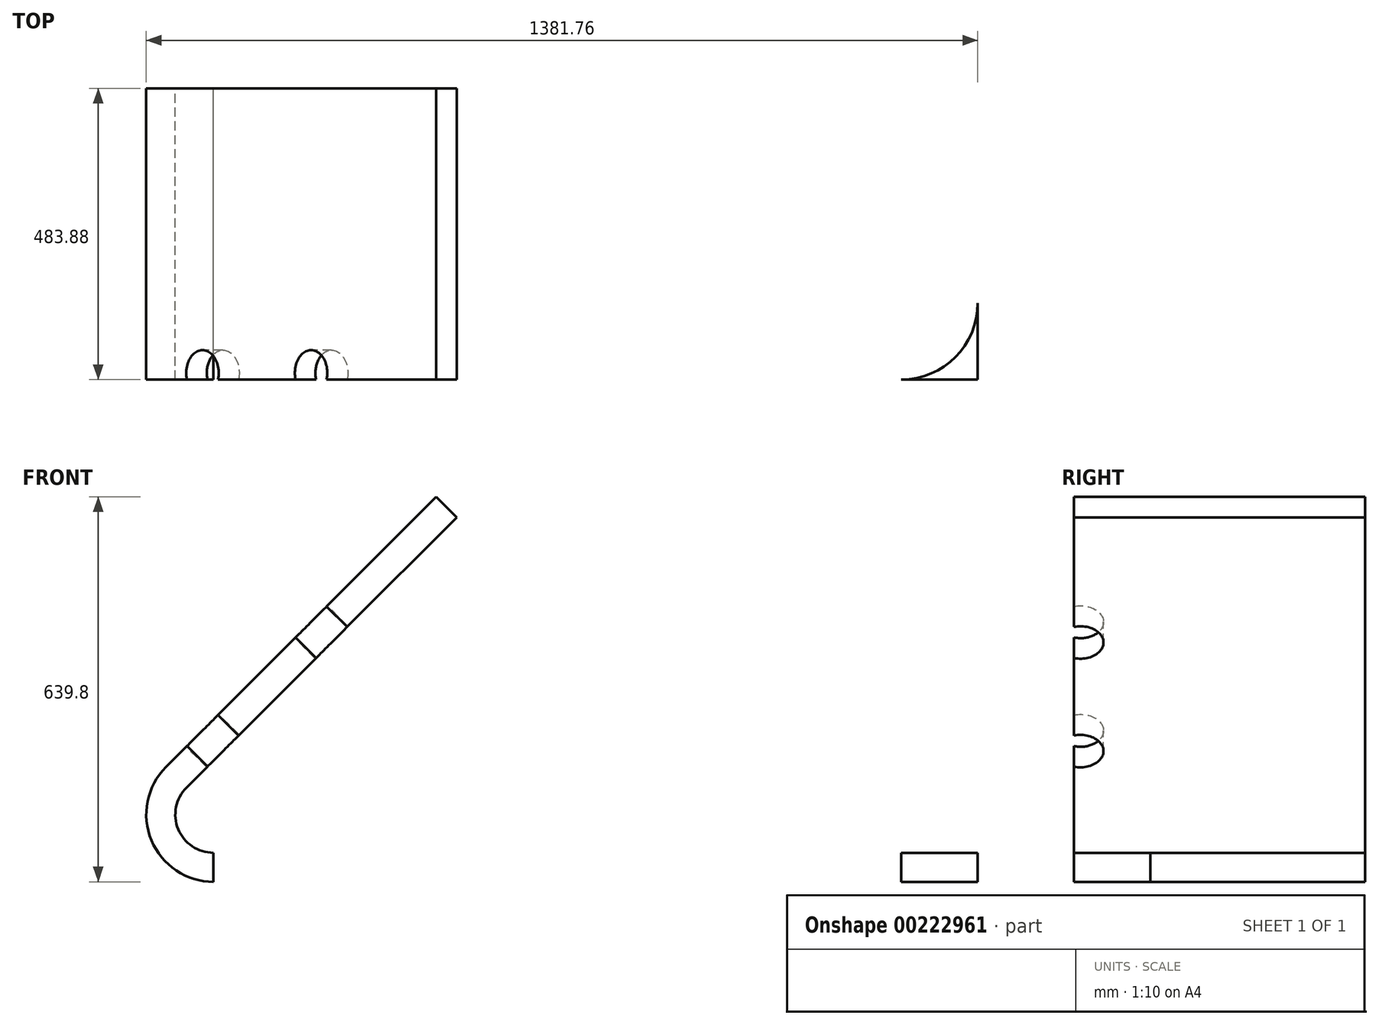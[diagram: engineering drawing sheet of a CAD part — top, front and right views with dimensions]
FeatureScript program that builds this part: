
annotation { "Feature Type Name" : "Feature", "Feature Type Description" : "" }
export const myFeature = defineFeature(function(context is Context, id is Id, definition is map)
    precondition{}
    {
        {
            var Q0;
            Q0=qCreatedBy(makeId("Front.planeOp"),FACE);
            var sketch = newSketch(context, id + "F0", { "sketchPlane" : qUnion([Q0])});
            skArc(sketch, "E0", {"start": v(-380.76, 79.03) * mm, "mid": v(-405, -42.77) * mm, "end": v(-301.74, -111.76) * mm});
            skLineSegment(sketch, "E1", {"start": v(-380.76, 79.03) * mm, "end": v(68.25, 528.04) * mm});
            skLineSegment(sketch, "E2", {"start": v(-301.74, -111.76) * mm, "end": v(968.26, -111.76) * mm});
            skLineSegment(sketch, "E3", {"start": v(968.26, -111.76) * mm, "end": v(968.26, -63.5) * mm});
            skLineSegment(sketch, "E4", {"start": v(102.37, 493.91) * mm, "end": v(68.25, 528.04) * mm});
            skLineSegment(sketch, "E5", {"start": v(968.26, -63.5) * mm, "end": v(-301.74, -63.5) * mm});
            skLineSegment(sketch, "E6", {"start": v(102.37, 493.91) * mm, "end": v(-346.64, 44.9) * mm});
            skArc(sketch, "E7", {"start": v(-346.64, 44.9) * mm, "mid": v(-360.4, -24.3) * mm, "end": v(-301.74, -63.5) * mm});
            skSolve(sketch);
        }
        {
            var Q0;
            Q0=makeQuery(id+"F0.imprint","IMPRINT",FACE,{"disambiguationData":[TD([[makeQuery(id+"F0.imprint","IMPRINT",EDGE,{"derivedFrom":sQuery(id+"F0.wireOp",EDGE,"E0")}),1.0]])]});
            extrude(context, id + "F1", {"entities" : qUnion([Q0]), "endBound" : BoundingType.SYMMETRIC, "depth" : 483.87 * mm});
        }
        {
            var Q0;
            Q0=makeQuery(id+"F1.opExtrude","SWEPT_FACE",FACE,{"disambiguationData":[OSD([sQuery(id+"F0.wireOp",EDGE,"E1")])]});
            var sketch = newSketch(context, id + "F2", { "sketchPlane" : qUnion([Q0])});
            skLineSegment(sketch, "E8", {"start": v(-325.12, -241.94) * mm, "end": v(-325.12, 241.94) * mm});
            skLineSegment(sketch, "E9", {"start": v(421.64, -241.94) * mm, "end": v(421.64, -127.64) * mm});
            skLineSegment(sketch, "E10", {"start": v(421.64, -127.64) * mm, "end": v(231.14, -127.64) * mm});
            skCircle(sketch, "E11", {"center": v(231.14, -127.64) * mm, "radius": 38.1 * mm});
            skLineSegment(sketch, "E12", {"start": v(421.64, 0) * mm, "end": v(29.41, 0) * mm});
            skCircle(sketch, "E13.MirrorC", {"center": v(231.14, 127.64) * mm, "radius": 38.1 * mm});
            skLineSegment(sketch, "E14", {"start": v(421.64, 241.94) * mm, "end": v(421.64, 114.94) * mm});
            skArc(sketch, "E15", {"start": v(421.64, 114.94) * mm, "mid": v(384.44, 204.74) * mm, "end": v(294.64, 241.94) * mm});
            skLineSegment(sketch, "E16", {"start": v(294.64, 241.94) * mm, "end": v(421.64, 241.94) * mm});
            skArc(sketch, "E17.MirrorCS", {"start": v(421.64, -114.94) * mm, "mid": v(384.44, -204.74) * mm, "end": v(294.64, -241.94) * mm});
            skLineSegment(sketch, "E18.MirrorCS", {"start": v(421.64, -241.94) * mm, "end": v(421.64, -114.94) * mm});
            skLineSegment(sketch, "E19.MirrorCS", {"start": v(294.64, -241.94) * mm, "end": v(421.64, -241.94) * mm});
            skSolve(sketch);
        }
        {
            var Q0;
            Q0 = qSketchRegion(id + "F2", true);
            extrude(context, id + "F3", {"entities" : qUnion([Q0]), "operationType" : NewBodyOperationType.REMOVE, "oppositeDirection" : true, "depth" : 63.5 * mm});
        }
        {
            var Q0;
            Q0=makeQuery(id+"F1.opExtrude","SWEPT_FACE",FACE,{"disambiguationData":[OSD([sQuery(id+"F0.wireOp",EDGE,"E5")])]});
            var sketch = newSketch(context, id + "F4", { "sketchPlane" : qUnion([Q0])});
            skCircle(sketch, "E20", {"center": v(155.46, 0) * mm, "radius": 63.5 * mm});
            skArc(sketch, "E21", {"start": v(790.46, -63.5) * mm, "mid": v(853.96, 0) * mm, "end": v(790.46, 63.5) * mm});
            skArc(sketch, "E22.MirrorCS", {"start": v(536.46, -63.5) * mm, "mid": v(472.96, 0) * mm, "end": v(536.46, 63.5) * mm});
            skLineSegment(sketch, "E23", {"start": v(536.46, 63.5) * mm, "end": v(790.46, 63.5) * mm});
            skLineSegment(sketch, "E24", {"start": v(536.46, -63.5) * mm, "end": v(790.46, -63.5) * mm});
            skLineSegment(sketch, "E25", {"start": v(968.26, 241.94) * mm, "end": v(968.26, 114.94) * mm});
            skArc(sketch, "E26", {"start": v(968.26, 114.94) * mm, "mid": v(931.06, 204.74) * mm, "end": v(841.26, 241.94) * mm});
            skLineSegment(sketch, "E27", {"start": v(841.26, 241.94) * mm, "end": v(968.26, 241.94) * mm});
            skPoint(sketch, "E28.endSnap0", {"position": v(968.26, 0) * mm});
            skArc(sketch, "E29.MirrorCS", {"start": v(968.26, -114.94) * mm, "mid": v(931.06, -204.74) * mm, "end": v(841.26, -241.94) * mm});
            skLineSegment(sketch, "E30.MirrorCS", {"start": v(968.26, -241.94) * mm, "end": v(968.26, -114.94) * mm});
            skLineSegment(sketch, "E31.MirrorCS", {"start": v(841.26, -241.94) * mm, "end": v(968.26, -241.94) * mm});
            skSolve(sketch);
        }
        {
            var Q0;
            Q0=makeQuery(id+"F4.imprint","IMPRINT",FACE,{"disambiguationData":[TD([[makeQuery(id+"F4.imprint","IMPRINT",EDGE,{"derivedFrom":sQuery(id+"F4.wireOp",EDGE,"E20")}),1.0]])]});
            var Q1;
            Q1=makeQuery(id+"F4.imprint","IMPRINT",FACE,{"disambiguationData":[TD([[makeQuery(id+"F4.imprint","IMPRINT",EDGE,{"derivedFrom":sQuery(id+"F4.wireOp",EDGE,"E21")}),1.0]])]});
            var Q2;
            Q2=makeQuery(id+"F4.imprint","IMPRINT",FACE,{"disambiguationData":[TD([[makeQuery(id+"F4.imprint","IMPRINT",EDGE,{"derivedFrom":sQuery(id+"F4.wireOp",EDGE,"E25")}),1.0]])]});
            var Q3;
            Q3=makeQuery(id+"F4.imprint","IMPRINT",FACE,{"disambiguationData":[TD([[makeQuery(id+"F4.imprint","IMPRINT",EDGE,{"derivedFrom":sQuery(id+"F4.wireOp",EDGE,"E29.MirrorCS")}),1.0]])]});
            extrude(context, id + "F5", {"entities" : qUnion([Q0, Q1, Q2, Q3]), "operationType" : NewBodyOperationType.REMOVE, "oppositeDirection" : true, "depth" : 50.8 * mm});
        }
    });
